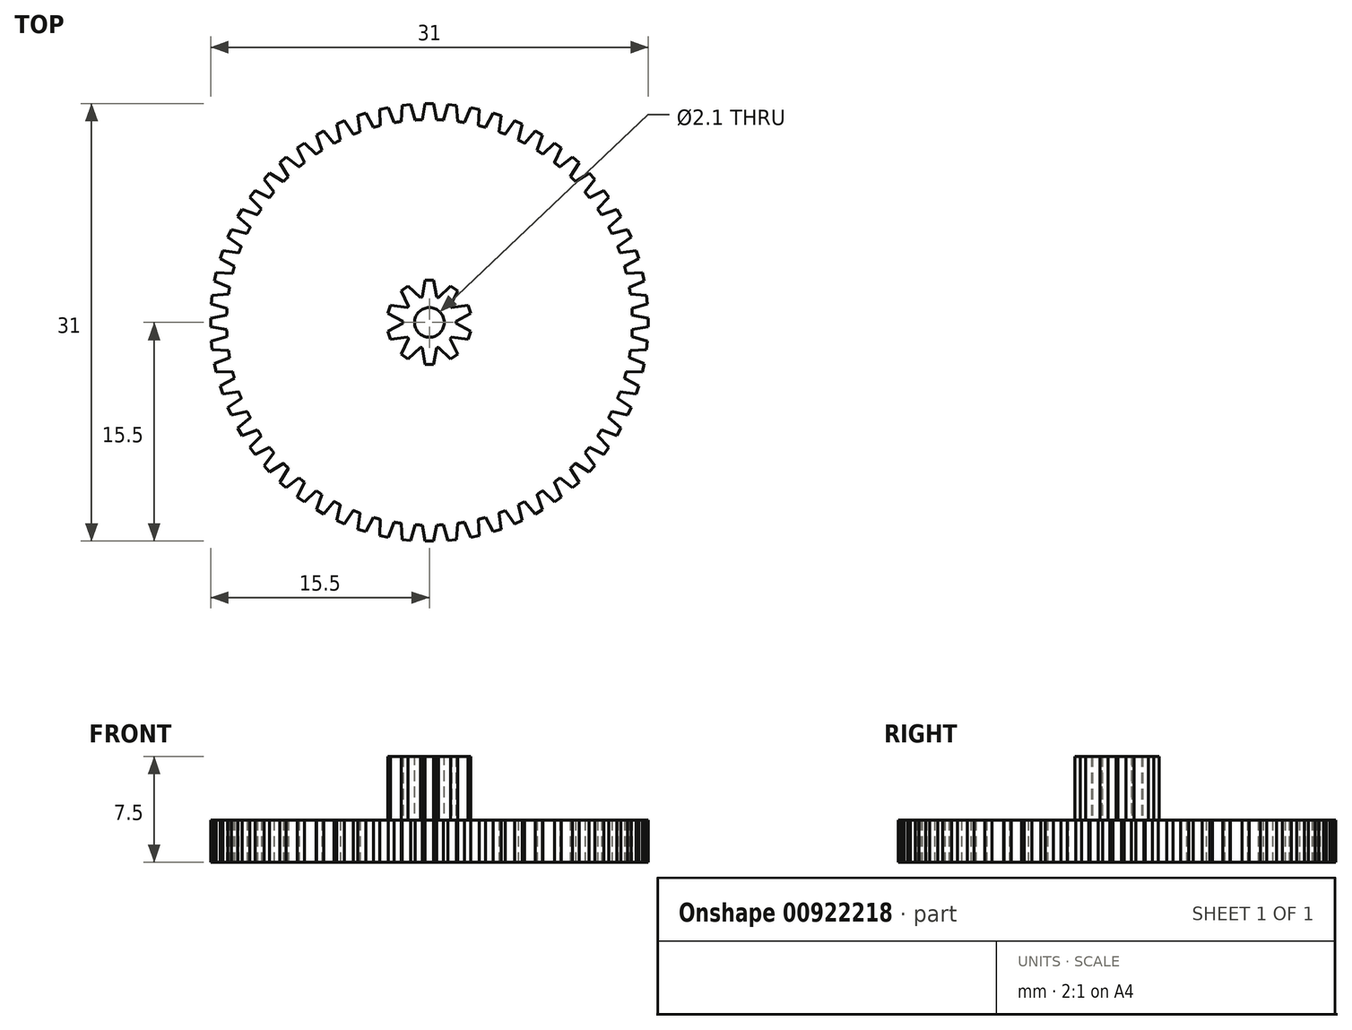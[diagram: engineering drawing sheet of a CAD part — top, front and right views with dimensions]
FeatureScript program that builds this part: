
annotation { "Feature Type Name" : "Feature", "Feature Type Description" : "" }
export const myFeature = defineFeature(function(context is Context, id is Id, definition is map)
    precondition{}
    {
        {
            var Q0;
            Q0=qCreatedBy(makeId("Top.planeOp"),FACE);
            var sketch = newSketch(context, id + "F0", { "sketchPlane" : qUnion([Q0])});
            skCircle(sketch, "E0", {"center": v(0, 0) * mm, "radius": 15 * mm, "construction": true});
            skCircle(sketch, "E1", {"center": v(0, 0) * mm, "radius": 15.5 * mm, "construction": true});
            skCircle(sketch, "E2", {"center": v(0, 0) * mm, "radius": 14.38 * mm});
            skLineSegment(sketch, "E3", {"start": v(0, 14.38) * mm, "end": v(0.5, 14.38) * mm, "construction": true});
            skLineSegment(sketch, "E4", {"start": v(0, 14.38) * mm, "end": v(-0.5, 14.38) * mm, "construction": true});
            skLineSegment(sketch, "E5", {"start": v(-1.79, 7.07) * mm, "end": v(-0.5, 14.37) * mm, "construction": true});
            skLineSegment(sketch, "E6", {"start": v(1.79, 7.07) * mm, "end": v(0.3, 15.5) * mm, "construction": true});
            skLineSegment(sketch, "E7", {"start": v(-1.79, 7.08) * mm, "end": v(-0.3, 15.5) * mm});
            skLineSegment(sketch, "E8", {"start": v(0.3, 15.5) * mm, "end": v(-0.3, 15.5) * mm});
            skLineSegment(sketch, "E9", {"start": v(0.3, 15.5) * mm, "end": v(0.5, 14.37) * mm});
            skLineSegment(sketch, "E10.1.0", {"start": v(-2.52, 6.85) * mm, "end": v(-1.92, 15.38) * mm});
            skLineSegment(sketch, "E10.1.1", {"start": v(-1.32, 15.44) * mm, "end": v(-1.92, 15.38) * mm});
            skLineSegment(sketch, "E10.1.2", {"start": v(-1.32, 15.44) * mm, "end": v(-1, 14.34) * mm});
            skLineSegment(sketch, "E10.2.0", {"start": v(-3.22, 6.55) * mm, "end": v(-3.52, 15.1) * mm});
            skLineSegment(sketch, "E10.2.1", {"start": v(-2.93, 15.22) * mm, "end": v(-3.52, 15.1) * mm});
            skLineSegment(sketch, "E10.2.2", {"start": v(-2.93, 15.22) * mm, "end": v(-2.5, 14.16) * mm});
            skLineSegment(sketch, "E11.1.3.0", {"start": v(-3.89, 6.18) * mm, "end": v(-5.08, 14.65) * mm});
            skLineSegment(sketch, "E11.3.3.0", {"start": v(-4.5, 14.83) * mm, "end": v(-5.08, 14.65) * mm});
            skLineSegment(sketch, "E11.6.3.0", {"start": v(-4.5, 14.83) * mm, "end": v(-3.96, 13.82) * mm});
            skLineSegment(sketch, "E11.1.4.0", {"start": v(-4.51, 5.74) * mm, "end": v(-6.58, 14.03) * mm});
            skLineSegment(sketch, "E11.3.4.0", {"start": v(-6.03, 14.28) * mm, "end": v(-6.58, 14.03) * mm});
            skLineSegment(sketch, "E11.6.4.0", {"start": v(-6.03, 14.28) * mm, "end": v(-5.39, 13.33) * mm});
            skLineSegment(sketch, "E11.1.5.0", {"start": v(-5.09, 5.24) * mm, "end": v(-8.01, 13.27) * mm});
            skLineSegment(sketch, "E11.3.5.0", {"start": v(-7.49, 13.57) * mm, "end": v(-8.01, 13.27) * mm});
            skLineSegment(sketch, "E11.6.5.0", {"start": v(-7.49, 13.57) * mm, "end": v(-6.75, 12.7) * mm});
            skLineSegment(sketch, "E11.1.6.0", {"start": v(-5.6, 4.68) * mm, "end": v(-9.35, 12.36) * mm});
            skLineSegment(sketch, "E11.3.6.0", {"start": v(-8.86, 12.71) * mm, "end": v(-9.35, 12.36) * mm});
            skLineSegment(sketch, "E11.6.6.0", {"start": v(-8.86, 12.71) * mm, "end": v(-8.04, 11.92) * mm});
            skLineSegment(sketch, "E11.1.7.0", {"start": v(-6.06, 4.07) * mm, "end": v(-10.6, 11.31) * mm});
            skLineSegment(sketch, "E11.3.7.0", {"start": v(-10.15, 11.72) * mm, "end": v(-10.6, 11.31) * mm});
            skLineSegment(sketch, "E11.6.7.0", {"start": v(-10.15, 11.72) * mm, "end": v(-9.24, 11.01) * mm});
            skLineSegment(sketch, "E11.1.8.0", {"start": v(-6.46, 3.4) * mm, "end": v(-11.72, 10.15) * mm});
            skLineSegment(sketch, "E11.3.8.0", {"start": v(-11.31, 10.6) * mm, "end": v(-11.72, 10.15) * mm});
            skLineSegment(sketch, "E11.6.8.0", {"start": v(-11.31, 10.6) * mm, "end": v(-10.34, 9.99) * mm});
            skLineSegment(sketch, "E11.1.9.0", {"start": v(-6.78, 2.72) * mm, "end": v(-12.71, 8.86) * mm});
            skLineSegment(sketch, "E11.3.9.0", {"start": v(-12.36, 9.35) * mm, "end": v(-12.71, 8.86) * mm});
            skLineSegment(sketch, "E11.6.9.0", {"start": v(-12.36, 9.35) * mm, "end": v(-11.33, 8.85) * mm});
            skLineSegment(sketch, "E11.1.10.0", {"start": v(-7.02, 2) * mm, "end": v(-13.57, 7.49) * mm});
            skLineSegment(sketch, "E11.3.10.0", {"start": v(-13.27, 8.01) * mm, "end": v(-13.57, 7.49) * mm});
            skLineSegment(sketch, "E11.6.10.0", {"start": v(-13.27, 8.01) * mm, "end": v(-12.2, 7.62) * mm});
            skLineSegment(sketch, "E11.1.11.0", {"start": v(-7.2, 1.25) * mm, "end": v(-14.28, 6.03) * mm});
            skLineSegment(sketch, "E11.3.11.0", {"start": v(-14.03, 6.58) * mm, "end": v(-14.28, 6.03) * mm});
            skLineSegment(sketch, "E11.6.11.0", {"start": v(-14.03, 6.58) * mm, "end": v(-12.92, 6.3) * mm});
            skLineSegment(sketch, "E11.1.12.0", {"start": v(-7.28, 0.49) * mm, "end": v(-14.83, 4.5) * mm});
            skLineSegment(sketch, "E11.3.12.0", {"start": v(-14.65, 5.08) * mm, "end": v(-14.83, 4.5) * mm});
            skLineSegment(sketch, "E11.6.12.0", {"start": v(-14.65, 5.08) * mm, "end": v(-13.5, 4.92) * mm});
            skLineSegment(sketch, "E11.1.13.0", {"start": v(-7.3, -0.28) * mm, "end": v(-15.22, 2.93) * mm});
            skLineSegment(sketch, "E11.3.13.0", {"start": v(-15.1, 3.52) * mm, "end": v(-15.22, 2.93) * mm});
            skLineSegment(sketch, "E11.6.13.0", {"start": v(-15.1, 3.52) * mm, "end": v(-13.95, 3.48) * mm});
            skLineSegment(sketch, "E11.1.14.0", {"start": v(-7.23, -1.04) * mm, "end": v(-15.44, 1.32) * mm});
            skLineSegment(sketch, "E11.3.14.0", {"start": v(-15.38, 1.92) * mm, "end": v(-15.44, 1.32) * mm});
            skLineSegment(sketch, "E11.6.14.0", {"start": v(-15.38, 1.92) * mm, "end": v(-14.24, 2) * mm});
            skLineSegment(sketch, "E11.1.15.0", {"start": v(-7.08, -1.79) * mm, "end": v(-15.5, -0.3) * mm});
            skLineSegment(sketch, "E11.3.15.0", {"start": v(-15.5, 0.3) * mm, "end": v(-15.5, -0.3) * mm});
            skLineSegment(sketch, "E11.6.15.0", {"start": v(-15.5, 0.3) * mm, "end": v(-14.37, 0.5) * mm});
            skLineSegment(sketch, "E11.1.16.0", {"start": v(-6.85, -2.52) * mm, "end": v(-15.38, -1.92) * mm});
            skLineSegment(sketch, "E11.3.16.0", {"start": v(-15.44, -1.32) * mm, "end": v(-15.38, -1.92) * mm});
            skLineSegment(sketch, "E11.6.16.0", {"start": v(-15.44, -1.32) * mm, "end": v(-14.34, -1) * mm});
            skLineSegment(sketch, "E11.1.17.0", {"start": v(-6.55, -3.22) * mm, "end": v(-15.1, -3.52) * mm});
            skLineSegment(sketch, "E11.3.17.0", {"start": v(-15.22, -2.93) * mm, "end": v(-15.1, -3.52) * mm});
            skLineSegment(sketch, "E11.6.17.0", {"start": v(-15.22, -2.93) * mm, "end": v(-14.16, -2.5) * mm});
            skLineSegment(sketch, "E11.1.18.0", {"start": v(-6.18, -3.89) * mm, "end": v(-14.65, -5.08) * mm});
            skLineSegment(sketch, "E11.3.18.0", {"start": v(-14.83, -4.5) * mm, "end": v(-14.65, -5.08) * mm});
            skLineSegment(sketch, "E11.6.18.0", {"start": v(-14.83, -4.5) * mm, "end": v(-13.82, -3.96) * mm});
            skLineSegment(sketch, "E11.1.19.0", {"start": v(-5.74, -4.51) * mm, "end": v(-14.03, -6.58) * mm});
            skLineSegment(sketch, "E11.3.19.0", {"start": v(-14.28, -6.03) * mm, "end": v(-14.03, -6.58) * mm});
            skLineSegment(sketch, "E11.6.19.0", {"start": v(-14.28, -6.03) * mm, "end": v(-13.33, -5.39) * mm});
            skLineSegment(sketch, "E11.1.20.0", {"start": v(-5.24, -5.09) * mm, "end": v(-13.27, -8.01) * mm});
            skLineSegment(sketch, "E11.3.20.0", {"start": v(-13.57, -7.49) * mm, "end": v(-13.27, -8.01) * mm});
            skLineSegment(sketch, "E11.6.20.0", {"start": v(-13.57, -7.49) * mm, "end": v(-12.7, -6.75) * mm});
            skLineSegment(sketch, "E11.1.21.0", {"start": v(-4.68, -5.6) * mm, "end": v(-12.36, -9.35) * mm});
            skLineSegment(sketch, "E11.3.21.0", {"start": v(-12.71, -8.86) * mm, "end": v(-12.36, -9.35) * mm});
            skLineSegment(sketch, "E11.6.21.0", {"start": v(-12.71, -8.86) * mm, "end": v(-11.92, -8.04) * mm});
            skLineSegment(sketch, "E11.1.22.0", {"start": v(-4.07, -6.06) * mm, "end": v(-11.31, -10.6) * mm});
            skLineSegment(sketch, "E11.3.22.0", {"start": v(-11.72, -10.15) * mm, "end": v(-11.31, -10.6) * mm});
            skLineSegment(sketch, "E11.6.22.0", {"start": v(-11.72, -10.15) * mm, "end": v(-11.01, -9.24) * mm});
            skLineSegment(sketch, "E11.1.23.0", {"start": v(-3.4, -6.46) * mm, "end": v(-10.15, -11.72) * mm});
            skLineSegment(sketch, "E11.3.23.0", {"start": v(-10.6, -11.31) * mm, "end": v(-10.15, -11.72) * mm});
            skLineSegment(sketch, "E11.6.23.0", {"start": v(-10.6, -11.31) * mm, "end": v(-9.99, -10.34) * mm});
            skLineSegment(sketch, "E11.1.24.0", {"start": v(-2.72, -6.78) * mm, "end": v(-8.86, -12.71) * mm});
            skLineSegment(sketch, "E11.3.24.0", {"start": v(-9.35, -12.36) * mm, "end": v(-8.86, -12.71) * mm});
            skLineSegment(sketch, "E11.6.24.0", {"start": v(-9.35, -12.36) * mm, "end": v(-8.85, -11.33) * mm});
            skLineSegment(sketch, "E11.1.25.0", {"start": v(-2, -7.02) * mm, "end": v(-7.49, -13.57) * mm});
            skLineSegment(sketch, "E11.3.25.0", {"start": v(-8.01, -13.27) * mm, "end": v(-7.49, -13.57) * mm});
            skLineSegment(sketch, "E11.6.25.0", {"start": v(-8.01, -13.27) * mm, "end": v(-7.62, -12.2) * mm});
            skLineSegment(sketch, "E11.1.26.0", {"start": v(-1.25, -7.2) * mm, "end": v(-6.03, -14.28) * mm});
            skLineSegment(sketch, "E11.3.26.0", {"start": v(-6.58, -14.03) * mm, "end": v(-6.03, -14.28) * mm});
            skLineSegment(sketch, "E11.6.26.0", {"start": v(-6.58, -14.03) * mm, "end": v(-6.3, -12.92) * mm});
            skLineSegment(sketch, "E11.1.27.0", {"start": v(-0.49, -7.28) * mm, "end": v(-4.5, -14.83) * mm});
            skLineSegment(sketch, "E11.3.27.0", {"start": v(-5.08, -14.65) * mm, "end": v(-4.5, -14.83) * mm});
            skLineSegment(sketch, "E11.6.27.0", {"start": v(-5.08, -14.65) * mm, "end": v(-4.92, -13.5) * mm});
            skLineSegment(sketch, "E11.1.28.0", {"start": v(0.28, -7.3) * mm, "end": v(-2.93, -15.22) * mm});
            skLineSegment(sketch, "E11.3.28.0", {"start": v(-3.52, -15.1) * mm, "end": v(-2.93, -15.22) * mm});
            skLineSegment(sketch, "E11.6.28.0", {"start": v(-3.52, -15.1) * mm, "end": v(-3.48, -13.95) * mm});
            skLineSegment(sketch, "E11.1.29.0", {"start": v(1.04, -7.23) * mm, "end": v(-1.32, -15.44) * mm});
            skLineSegment(sketch, "E11.3.29.0", {"start": v(-1.92, -15.38) * mm, "end": v(-1.32, -15.44) * mm});
            skLineSegment(sketch, "E11.6.29.0", {"start": v(-1.92, -15.38) * mm, "end": v(-2, -14.24) * mm});
            skLineSegment(sketch, "E12.1.30.0", {"start": v(1.79, -7.08) * mm, "end": v(0.3, -15.5) * mm});
            skLineSegment(sketch, "E12.3.30.0", {"start": v(-0.3, -15.5) * mm, "end": v(0.3, -15.5) * mm});
            skLineSegment(sketch, "E12.6.30.0", {"start": v(-0.3, -15.5) * mm, "end": v(-0.5, -14.37) * mm});
            skLineSegment(sketch, "E12.1.31.0", {"start": v(2.52, -6.85) * mm, "end": v(1.92, -15.38) * mm});
            skLineSegment(sketch, "E12.3.31.0", {"start": v(1.32, -15.44) * mm, "end": v(1.92, -15.38) * mm});
            skLineSegment(sketch, "E12.6.31.0", {"start": v(1.32, -15.44) * mm, "end": v(1, -14.34) * mm});
            skLineSegment(sketch, "E12.1.32.0", {"start": v(3.22, -6.55) * mm, "end": v(3.52, -15.1) * mm});
            skLineSegment(sketch, "E12.3.32.0", {"start": v(2.93, -15.22) * mm, "end": v(3.52, -15.1) * mm});
            skLineSegment(sketch, "E12.6.32.0", {"start": v(2.93, -15.22) * mm, "end": v(2.5, -14.16) * mm});
            skLineSegment(sketch, "E12.1.33.0", {"start": v(3.89, -6.18) * mm, "end": v(5.08, -14.65) * mm});
            skLineSegment(sketch, "E12.3.33.0", {"start": v(4.5, -14.83) * mm, "end": v(5.08, -14.65) * mm});
            skLineSegment(sketch, "E12.6.33.0", {"start": v(4.5, -14.83) * mm, "end": v(3.96, -13.82) * mm});
            skLineSegment(sketch, "E12.1.34.0", {"start": v(4.51, -5.74) * mm, "end": v(6.58, -14.03) * mm});
            skLineSegment(sketch, "E12.3.34.0", {"start": v(6.03, -14.28) * mm, "end": v(6.58, -14.03) * mm});
            skLineSegment(sketch, "E12.6.34.0", {"start": v(6.03, -14.28) * mm, "end": v(5.39, -13.33) * mm});
            skLineSegment(sketch, "E12.1.35.0", {"start": v(5.09, -5.24) * mm, "end": v(8.01, -13.27) * mm});
            skLineSegment(sketch, "E12.3.35.0", {"start": v(7.49, -13.57) * mm, "end": v(8.01, -13.27) * mm});
            skLineSegment(sketch, "E12.6.35.0", {"start": v(7.49, -13.57) * mm, "end": v(6.75, -12.7) * mm});
            skLineSegment(sketch, "E12.1.36.0", {"start": v(5.6, -4.68) * mm, "end": v(9.35, -12.36) * mm});
            skLineSegment(sketch, "E12.3.36.0", {"start": v(8.86, -12.71) * mm, "end": v(9.35, -12.36) * mm});
            skLineSegment(sketch, "E12.6.36.0", {"start": v(8.86, -12.71) * mm, "end": v(8.04, -11.92) * mm});
            skLineSegment(sketch, "E12.1.37.0", {"start": v(6.06, -4.07) * mm, "end": v(10.6, -11.31) * mm});
            skLineSegment(sketch, "E12.3.37.0", {"start": v(10.15, -11.72) * mm, "end": v(10.6, -11.31) * mm});
            skLineSegment(sketch, "E12.6.37.0", {"start": v(10.15, -11.72) * mm, "end": v(9.24, -11.01) * mm});
            skLineSegment(sketch, "E12.1.38.0", {"start": v(6.46, -3.4) * mm, "end": v(11.72, -10.15) * mm});
            skLineSegment(sketch, "E12.3.38.0", {"start": v(11.31, -10.6) * mm, "end": v(11.72, -10.15) * mm});
            skLineSegment(sketch, "E12.6.38.0", {"start": v(11.31, -10.6) * mm, "end": v(10.34, -9.99) * mm});
            skLineSegment(sketch, "E12.1.39.0", {"start": v(6.78, -2.72) * mm, "end": v(12.71, -8.86) * mm});
            skLineSegment(sketch, "E12.3.39.0", {"start": v(12.36, -9.35) * mm, "end": v(12.71, -8.86) * mm});
            skLineSegment(sketch, "E12.6.39.0", {"start": v(12.36, -9.35) * mm, "end": v(11.33, -8.85) * mm});
            skLineSegment(sketch, "E12.1.40.0", {"start": v(7.02, -2) * mm, "end": v(13.57, -7.49) * mm});
            skLineSegment(sketch, "E12.3.40.0", {"start": v(13.27, -8.01) * mm, "end": v(13.57, -7.49) * mm});
            skLineSegment(sketch, "E12.6.40.0", {"start": v(13.27, -8.01) * mm, "end": v(12.2, -7.62) * mm});
            skLineSegment(sketch, "E12.1.41.0", {"start": v(7.2, -1.25) * mm, "end": v(14.28, -6.03) * mm});
            skLineSegment(sketch, "E12.3.41.0", {"start": v(14.03, -6.58) * mm, "end": v(14.28, -6.03) * mm});
            skLineSegment(sketch, "E12.6.41.0", {"start": v(14.03, -6.58) * mm, "end": v(12.92, -6.3) * mm});
            skLineSegment(sketch, "E13.1.42.0", {"start": v(7.28, -0.49) * mm, "end": v(14.83, -4.5) * mm});
            skLineSegment(sketch, "E13.3.42.0", {"start": v(14.65, -5.08) * mm, "end": v(14.83, -4.5) * mm});
            skLineSegment(sketch, "E13.6.42.0", {"start": v(14.65, -5.08) * mm, "end": v(13.5, -4.92) * mm});
            skLineSegment(sketch, "E13.1.43.0", {"start": v(7.3, 0.28) * mm, "end": v(15.22, -2.93) * mm});
            skLineSegment(sketch, "E13.3.43.0", {"start": v(15.1, -3.52) * mm, "end": v(15.22, -2.93) * mm});
            skLineSegment(sketch, "E13.6.43.0", {"start": v(15.1, -3.52) * mm, "end": v(13.95, -3.48) * mm});
            skLineSegment(sketch, "E13.1.44.0", {"start": v(7.23, 1.04) * mm, "end": v(15.44, -1.32) * mm});
            skLineSegment(sketch, "E13.3.44.0", {"start": v(15.38, -1.92) * mm, "end": v(15.44, -1.32) * mm});
            skLineSegment(sketch, "E13.6.44.0", {"start": v(15.38, -1.92) * mm, "end": v(14.24, -2) * mm});
            skLineSegment(sketch, "E13.1.45.0", {"start": v(7.08, 1.79) * mm, "end": v(15.5, 0.3) * mm});
            skLineSegment(sketch, "E13.3.45.0", {"start": v(15.5, -0.3) * mm, "end": v(15.5, 0.3) * mm});
            skLineSegment(sketch, "E13.6.45.0", {"start": v(15.5, -0.3) * mm, "end": v(14.37, -0.5) * mm});
            skLineSegment(sketch, "E13.1.46.0", {"start": v(6.85, 2.52) * mm, "end": v(15.38, 1.92) * mm});
            skLineSegment(sketch, "E13.3.46.0", {"start": v(15.44, 1.32) * mm, "end": v(15.38, 1.92) * mm});
            skLineSegment(sketch, "E13.6.46.0", {"start": v(15.44, 1.32) * mm, "end": v(14.34, 1) * mm});
            skLineSegment(sketch, "E13.1.47.0", {"start": v(6.55, 3.22) * mm, "end": v(15.1, 3.52) * mm});
            skLineSegment(sketch, "E13.3.47.0", {"start": v(15.22, 2.93) * mm, "end": v(15.1, 3.52) * mm});
            skLineSegment(sketch, "E13.6.47.0", {"start": v(15.22, 2.93) * mm, "end": v(14.16, 2.5) * mm});
            skLineSegment(sketch, "E14.1.48.0", {"start": v(6.18, 3.89) * mm, "end": v(14.65, 5.08) * mm});
            skLineSegment(sketch, "E14.3.48.0", {"start": v(14.83, 4.5) * mm, "end": v(14.65, 5.08) * mm});
            skLineSegment(sketch, "E14.6.48.0", {"start": v(14.83, 4.5) * mm, "end": v(13.82, 3.96) * mm});
            skLineSegment(sketch, "E14.1.49.0", {"start": v(5.74, 4.51) * mm, "end": v(14.03, 6.58) * mm});
            skLineSegment(sketch, "E14.3.49.0", {"start": v(14.28, 6.03) * mm, "end": v(14.03, 6.58) * mm});
            skLineSegment(sketch, "E14.6.49.0", {"start": v(14.28, 6.03) * mm, "end": v(13.33, 5.39) * mm});
            skLineSegment(sketch, "E14.1.50.0", {"start": v(5.24, 5.09) * mm, "end": v(13.27, 8.01) * mm});
            skLineSegment(sketch, "E14.3.50.0", {"start": v(13.57, 7.49) * mm, "end": v(13.27, 8.01) * mm});
            skLineSegment(sketch, "E14.6.50.0", {"start": v(13.57, 7.49) * mm, "end": v(12.7, 6.75) * mm});
            skLineSegment(sketch, "E14.1.51.0", {"start": v(4.68, 5.6) * mm, "end": v(12.36, 9.35) * mm});
            skLineSegment(sketch, "E14.3.51.0", {"start": v(12.71, 8.86) * mm, "end": v(12.36, 9.35) * mm});
            skLineSegment(sketch, "E14.6.51.0", {"start": v(12.71, 8.86) * mm, "end": v(11.92, 8.04) * mm});
            skLineSegment(sketch, "E14.1.52.0", {"start": v(4.07, 6.06) * mm, "end": v(11.31, 10.6) * mm});
            skLineSegment(sketch, "E14.3.52.0", {"start": v(11.72, 10.15) * mm, "end": v(11.31, 10.6) * mm});
            skLineSegment(sketch, "E14.6.52.0", {"start": v(11.72, 10.15) * mm, "end": v(11.01, 9.24) * mm});
            skLineSegment(sketch, "E14.1.53.0", {"start": v(3.4, 6.46) * mm, "end": v(10.15, 11.72) * mm});
            skLineSegment(sketch, "E14.3.53.0", {"start": v(10.6, 11.31) * mm, "end": v(10.15, 11.72) * mm});
            skLineSegment(sketch, "E14.6.53.0", {"start": v(10.6, 11.31) * mm, "end": v(9.99, 10.34) * mm});
            skLineSegment(sketch, "E15.1.54.0", {"start": v(2.72, 6.78) * mm, "end": v(8.86, 12.71) * mm});
            skLineSegment(sketch, "E15.3.54.0", {"start": v(9.35, 12.36) * mm, "end": v(8.86, 12.71) * mm});
            skLineSegment(sketch, "E15.6.54.0", {"start": v(9.35, 12.36) * mm, "end": v(8.85, 11.33) * mm});
            skLineSegment(sketch, "E15.1.55.0", {"start": v(2, 7.02) * mm, "end": v(7.49, 13.57) * mm});
            skLineSegment(sketch, "E15.3.55.0", {"start": v(8.01, 13.27) * mm, "end": v(7.49, 13.57) * mm});
            skLineSegment(sketch, "E15.6.55.0", {"start": v(8.01, 13.27) * mm, "end": v(7.62, 12.2) * mm});
            skLineSegment(sketch, "E15.1.56.0", {"start": v(1.25, 7.2) * mm, "end": v(6.03, 14.28) * mm});
            skLineSegment(sketch, "E15.3.56.0", {"start": v(6.58, 14.03) * mm, "end": v(6.03, 14.28) * mm});
            skLineSegment(sketch, "E15.6.56.0", {"start": v(6.58, 14.03) * mm, "end": v(6.3, 12.92) * mm});
            skLineSegment(sketch, "E15.1.57.0", {"start": v(0.49, 7.28) * mm, "end": v(4.5, 14.83) * mm});
            skLineSegment(sketch, "E15.3.57.0", {"start": v(5.08, 14.65) * mm, "end": v(4.5, 14.83) * mm});
            skLineSegment(sketch, "E15.6.57.0", {"start": v(5.08, 14.65) * mm, "end": v(4.92, 13.5) * mm});
            skLineSegment(sketch, "E15.1.58.0", {"start": v(-0.28, 7.3) * mm, "end": v(2.93, 15.22) * mm});
            skLineSegment(sketch, "E15.3.58.0", {"start": v(3.52, 15.1) * mm, "end": v(2.93, 15.22) * mm});
            skLineSegment(sketch, "E15.6.58.0", {"start": v(3.52, 15.1) * mm, "end": v(3.48, 13.95) * mm});
            skLineSegment(sketch, "E15.1.59.0", {"start": v(-1.04, 7.23) * mm, "end": v(1.32, 15.44) * mm});
            skLineSegment(sketch, "E15.3.59.0", {"start": v(1.92, 15.38) * mm, "end": v(1.32, 15.44) * mm});
            skLineSegment(sketch, "E15.6.59.0", {"start": v(1.92, 15.38) * mm, "end": v(2, 14.24) * mm});
            skSolve(sketch);
        }
        {
            var Q0;
            Q0=qSketchRegion(id+"F0",true);
            extrude(context, id + "F1", {"entities" : qUnion([Q0]), "depth" : 3 * mm, "offsetDistance" : 25 * mm});
        }
        {
            var Q0;
            Q0=makeQuery(id+"F1.opExtrude","CAP_FACE",FACE,{"disambiguationData":[OSD([sQuery(id+"F0.wireOp",EDGE,"E2"),sQuery(id+"F0.wireOp",EDGE,"E7"),sQuery(id+"F0.wireOp",EDGE,"E8"),sQuery(id+"F0.wireOp",EDGE,"E9"),sQuery(id+"F0.wireOp",EDGE,"E10.1.0"),sQuery(id+"F0.wireOp",EDGE,"E10.1.1"),sQuery(id+"F0.wireOp",EDGE,"E10.1.2"),sQuery(id+"F0.wireOp",EDGE,"E10.2.0"),sQuery(id+"F0.wireOp",EDGE,"E10.2.1"),sQuery(id+"F0.wireOp",EDGE,"E10.2.2"),sQuery(id+"F0.wireOp",EDGE,"E11.1.3.0"),sQuery(id+"F0.wireOp",EDGE,"E11.3.3.0"),sQuery(id+"F0.wireOp",EDGE,"E11.6.3.0"),sQuery(id+"F0.wireOp",EDGE,"E11.1.4.0"),sQuery(id+"F0.wireOp",EDGE,"E11.3.4.0"),sQuery(id+"F0.wireOp",EDGE,"E11.6.4.0"),sQuery(id+"F0.wireOp",EDGE,"E11.1.5.0"),sQuery(id+"F0.wireOp",EDGE,"E11.3.5.0"),sQuery(id+"F0.wireOp",EDGE,"E11.6.5.0"),sQuery(id+"F0.wireOp",EDGE,"E11.1.6.0"),sQuery(id+"F0.wireOp",EDGE,"E11.3.6.0"),sQuery(id+"F0.wireOp",EDGE,"E11.6.6.0"),sQuery(id+"F0.wireOp",EDGE,"E11.1.7.0"),sQuery(id+"F0.wireOp",EDGE,"E11.3.7.0"),sQuery(id+"F0.wireOp",EDGE,"E11.6.7.0"),sQuery(id+"F0.wireOp",EDGE,"E11.1.8.0"),sQuery(id+"F0.wireOp",EDGE,"E11.3.8.0"),sQuery(id+"F0.wireOp",EDGE,"E11.6.8.0"),sQuery(id+"F0.wireOp",EDGE,"E11.1.9.0"),sQuery(id+"F0.wireOp",EDGE,"E11.3.9.0"),sQuery(id+"F0.wireOp",EDGE,"E11.6.9.0"),sQuery(id+"F0.wireOp",EDGE,"E11.1.10.0"),sQuery(id+"F0.wireOp",EDGE,"E11.3.10.0"),sQuery(id+"F0.wireOp",EDGE,"E11.6.10.0"),sQuery(id+"F0.wireOp",EDGE,"E11.1.11.0"),sQuery(id+"F0.wireOp",EDGE,"E11.3.11.0"),sQuery(id+"F0.wireOp",EDGE,"E11.6.11.0"),sQuery(id+"F0.wireOp",EDGE,"E11.1.12.0"),sQuery(id+"F0.wireOp",EDGE,"E11.3.12.0"),sQuery(id+"F0.wireOp",EDGE,"E11.6.12.0"),sQuery(id+"F0.wireOp",EDGE,"E11.1.13.0"),sQuery(id+"F0.wireOp",EDGE,"E11.3.13.0"),sQuery(id+"F0.wireOp",EDGE,"E11.6.13.0"),sQuery(id+"F0.wireOp",EDGE,"E11.1.14.0"),sQuery(id+"F0.wireOp",EDGE,"E11.3.14.0"),sQuery(id+"F0.wireOp",EDGE,"E11.6.14.0"),sQuery(id+"F0.wireOp",EDGE,"E11.1.15.0"),sQuery(id+"F0.wireOp",EDGE,"E11.3.15.0"),sQuery(id+"F0.wireOp",EDGE,"E11.6.15.0"),sQuery(id+"F0.wireOp",EDGE,"E11.1.16.0"),sQuery(id+"F0.wireOp",EDGE,"E11.3.16.0"),sQuery(id+"F0.wireOp",EDGE,"E11.6.16.0"),sQuery(id+"F0.wireOp",EDGE,"E11.1.17.0"),sQuery(id+"F0.wireOp",EDGE,"E11.3.17.0"),sQuery(id+"F0.wireOp",EDGE,"E11.6.17.0"),sQuery(id+"F0.wireOp",EDGE,"E11.1.18.0"),sQuery(id+"F0.wireOp",EDGE,"E11.3.18.0"),sQuery(id+"F0.wireOp",EDGE,"E11.6.18.0"),sQuery(id+"F0.wireOp",EDGE,"E11.1.19.0"),sQuery(id+"F0.wireOp",EDGE,"E11.3.19.0"),sQuery(id+"F0.wireOp",EDGE,"E11.6.19.0"),sQuery(id+"F0.wireOp",EDGE,"E11.1.20.0"),sQuery(id+"F0.wireOp",EDGE,"E11.3.20.0"),sQuery(id+"F0.wireOp",EDGE,"E11.6.20.0"),sQuery(id+"F0.wireOp",EDGE,"E11.1.21.0"),sQuery(id+"F0.wireOp",EDGE,"E11.3.21.0"),sQuery(id+"F0.wireOp",EDGE,"E11.6.21.0"),sQuery(id+"F0.wireOp",EDGE,"E11.1.22.0"),sQuery(id+"F0.wireOp",EDGE,"E11.3.22.0"),sQuery(id+"F0.wireOp",EDGE,"E11.6.22.0"),sQuery(id+"F0.wireOp",EDGE,"E11.1.23.0"),sQuery(id+"F0.wireOp",EDGE,"E11.3.23.0"),sQuery(id+"F0.wireOp",EDGE,"E11.6.23.0"),sQuery(id+"F0.wireOp",EDGE,"E11.1.24.0"),sQuery(id+"F0.wireOp",EDGE,"E11.3.24.0"),sQuery(id+"F0.wireOp",EDGE,"E11.6.24.0"),sQuery(id+"F0.wireOp",EDGE,"E11.1.25.0"),sQuery(id+"F0.wireOp",EDGE,"E11.3.25.0"),sQuery(id+"F0.wireOp",EDGE,"E11.6.25.0"),sQuery(id+"F0.wireOp",EDGE,"E11.1.26.0"),sQuery(id+"F0.wireOp",EDGE,"E11.3.26.0"),sQuery(id+"F0.wireOp",EDGE,"E11.6.26.0"),sQuery(id+"F0.wireOp",EDGE,"E11.1.27.0"),sQuery(id+"F0.wireOp",EDGE,"E11.3.27.0"),sQuery(id+"F0.wireOp",EDGE,"E11.6.27.0"),sQuery(id+"F0.wireOp",EDGE,"E11.1.28.0"),sQuery(id+"F0.wireOp",EDGE,"E11.3.28.0"),sQuery(id+"F0.wireOp",EDGE,"E11.6.28.0"),sQuery(id+"F0.wireOp",EDGE,"E11.1.29.0"),sQuery(id+"F0.wireOp",EDGE,"E11.3.29.0"),sQuery(id+"F0.wireOp",EDGE,"E11.6.29.0")])],"isStart":false});
            var sketch = newSketch(context, id + "F2", { "sketchPlane" : qUnion([Q0])});
            skCircle(sketch, "E16", {"center": v(0, 0) * mm, "radius": 2.5 * mm, "construction": true});
            skCircle(sketch, "E17", {"center": v(0, 0) * mm, "radius": 3 * mm, "construction": true});
            skCircle(sketch, "E18", {"center": v(0, 0) * mm, "radius": 1.88 * mm});
            skLineSegment(sketch, "E19", {"start": v(0, 1.88) * mm, "end": v(0.5, 1.88) * mm, "construction": true});
            skLineSegment(sketch, "E20", {"start": v(0, 1.88) * mm, "end": v(-0.5, 1.88) * mm, "construction": true});
            skLineSegment(sketch, "E21", {"start": v(-0.51, 1.8) * mm, "end": v(-0.3, 2.98) * mm, "construction": true});
            skLineSegment(sketch, "E22", {"start": v(0.51, 1.8) * mm, "end": v(0.3, 2.98) * mm, "construction": true});
            skLineSegment(sketch, "E23", {"start": v(-0.51, 1.8) * mm, "end": v(-0.3, 2.98) * mm});
            skLineSegment(sketch, "E24", {"start": v(0.3, 2.98) * mm, "end": v(-0.3, 2.98) * mm});
            skLineSegment(sketch, "E25", {"start": v(0.3, 2.98) * mm, "end": v(0.51, 1.8) * mm});
            skLineSegment(sketch, "E26.1.0", {"start": v(-1.47, 1.16) * mm, "end": v(-2, 2.24) * mm});
            skLineSegment(sketch, "E26.1.1", {"start": v(-1.5, 2.6) * mm, "end": v(-2, 2.24) * mm});
            skLineSegment(sketch, "E26.1.2", {"start": v(-1.5, 2.6) * mm, "end": v(-0.65, 1.76) * mm});
            skLineSegment(sketch, "E26.2.0", {"start": v(-1.87, 0.07) * mm, "end": v(-2.93, 0.63) * mm});
            skLineSegment(sketch, "E26.2.1", {"start": v(-2.74, 1.21) * mm, "end": v(-2.93, 0.63) * mm});
            skLineSegment(sketch, "E26.2.2", {"start": v(-2.74, 1.21) * mm, "end": v(-1.56, 1.04) * mm});
            skLineSegment(sketch, "E27.1.3.0", {"start": v(-1.56, -1.04) * mm, "end": v(-2.74, -1.21) * mm});
            skLineSegment(sketch, "E27.3.3.0", {"start": v(-2.93, -0.63) * mm, "end": v(-2.74, -1.21) * mm});
            skLineSegment(sketch, "E27.6.3.0", {"start": v(-2.93, -0.63) * mm, "end": v(-1.87, -0.07) * mm});
            skLineSegment(sketch, "E27.1.4.0", {"start": v(-0.65, -1.76) * mm, "end": v(-1.5, -2.6) * mm});
            skLineSegment(sketch, "E27.3.4.0", {"start": v(-2, -2.24) * mm, "end": v(-1.5, -2.6) * mm});
            skLineSegment(sketch, "E27.6.4.0", {"start": v(-2, -2.24) * mm, "end": v(-1.47, -1.16) * mm});
            skLineSegment(sketch, "E27.1.5.0", {"start": v(0.51, -1.8) * mm, "end": v(0.3, -2.98) * mm});
            skLineSegment(sketch, "E27.3.5.0", {"start": v(-0.3, -2.98) * mm, "end": v(0.3, -2.98) * mm});
            skLineSegment(sketch, "E27.6.5.0", {"start": v(-0.3, -2.98) * mm, "end": v(-0.51, -1.8) * mm});
            skLineSegment(sketch, "E27.1.6.0", {"start": v(1.47, -1.16) * mm, "end": v(2, -2.24) * mm});
            skLineSegment(sketch, "E27.3.6.0", {"start": v(1.5, -2.6) * mm, "end": v(2, -2.24) * mm});
            skLineSegment(sketch, "E27.6.6.0", {"start": v(1.5, -2.6) * mm, "end": v(0.65, -1.76) * mm});
            skLineSegment(sketch, "E27.1.7.0", {"start": v(1.87, -0.07) * mm, "end": v(2.93, -0.63) * mm});
            skLineSegment(sketch, "E27.3.7.0", {"start": v(2.74, -1.21) * mm, "end": v(2.93, -0.63) * mm});
            skLineSegment(sketch, "E27.6.7.0", {"start": v(2.74, -1.21) * mm, "end": v(1.56, -1.04) * mm});
            skLineSegment(sketch, "E27.1.8.0", {"start": v(1.56, 1.04) * mm, "end": v(2.74, 1.21) * mm});
            skLineSegment(sketch, "E27.3.8.0", {"start": v(2.93, 0.63) * mm, "end": v(2.74, 1.21) * mm});
            skLineSegment(sketch, "E27.6.8.0", {"start": v(2.93, 0.63) * mm, "end": v(1.87, 0.07) * mm});
            skLineSegment(sketch, "E27.1.9.0", {"start": v(0.65, 1.76) * mm, "end": v(1.5, 2.6) * mm});
            skLineSegment(sketch, "E27.3.9.0", {"start": v(2, 2.24) * mm, "end": v(1.5, 2.6) * mm});
            skLineSegment(sketch, "E27.6.9.0", {"start": v(2, 2.24) * mm, "end": v(1.47, 1.16) * mm});
            skSolve(sketch);
        }
        {
            var Q0;
            Q0=qSketchRegion(id+"F2",true);
            extrude(context, id + "F3", {"entities" : qUnion([Q0]), "operationType" : NewBodyOperationType.ADD, "depth" : 4.5 * mm, "offsetDistance" : 25 * mm});
        }
        {
            var Q0;
            Q0=makeQuery(id+"F3.opExtrude","CAP_FACE",FACE,{"disambiguationData":[OSD([sQuery(id+"F2.wireOp",EDGE,"E18"),sQuery(id+"F2.wireOp",EDGE,"E23"),sQuery(id+"F2.wireOp",EDGE,"E24"),sQuery(id+"F2.wireOp",EDGE,"E25"),sQuery(id+"F2.wireOp",EDGE,"E26.1.0"),sQuery(id+"F2.wireOp",EDGE,"E26.1.1"),sQuery(id+"F2.wireOp",EDGE,"E26.1.2"),sQuery(id+"F2.wireOp",EDGE,"E26.2.0"),sQuery(id+"F2.wireOp",EDGE,"E26.2.1"),sQuery(id+"F2.wireOp",EDGE,"E26.2.2"),sQuery(id+"F2.wireOp",EDGE,"E27.1.3.0"),sQuery(id+"F2.wireOp",EDGE,"E27.3.3.0"),sQuery(id+"F2.wireOp",EDGE,"E27.6.3.0"),sQuery(id+"F2.wireOp",EDGE,"E27.1.4.0"),sQuery(id+"F2.wireOp",EDGE,"E27.3.4.0"),sQuery(id+"F2.wireOp",EDGE,"E27.6.4.0"),sQuery(id+"F2.wireOp",EDGE,"E27.1.5.0"),sQuery(id+"F2.wireOp",EDGE,"E27.3.5.0"),sQuery(id+"F2.wireOp",EDGE,"E27.6.5.0"),sQuery(id+"F2.wireOp",EDGE,"E27.1.6.0"),sQuery(id+"F2.wireOp",EDGE,"E27.3.6.0"),sQuery(id+"F2.wireOp",EDGE,"E27.6.6.0"),sQuery(id+"F2.wireOp",EDGE,"E27.1.7.0"),sQuery(id+"F2.wireOp",EDGE,"E27.3.7.0"),sQuery(id+"F2.wireOp",EDGE,"E27.6.7.0"),sQuery(id+"F2.wireOp",EDGE,"E27.1.8.0"),sQuery(id+"F2.wireOp",EDGE,"E27.3.8.0"),sQuery(id+"F2.wireOp",EDGE,"E27.6.8.0"),sQuery(id+"F2.wireOp",EDGE,"E27.1.9.0"),sQuery(id+"F2.wireOp",EDGE,"E27.3.9.0"),sQuery(id+"F2.wireOp",EDGE,"E27.6.9.0")])],"isStart":false});
            var sketch = newSketch(context, id + "F4", { "sketchPlane" : qUnion([Q0])});
            skCircle(sketch, "E28", {"center": v(0, 0) * mm, "radius": 1.05 * mm});
            skSolve(sketch);
        }
        {
            var Q0;
            Q0=qSketchRegion(id+"F4",true);
            extrude(context, id + "F5", {"entities" : qUnion([Q0]), "operationType" : NewBodyOperationType.REMOVE, "endBound" : BoundingType.THROUGH_ALL, "oppositeDirection" : true, "depth" : 25 * mm, "offsetDistance" : 25 * mm});
        }
    });
